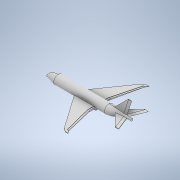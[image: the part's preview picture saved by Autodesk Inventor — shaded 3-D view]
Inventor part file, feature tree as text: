
AUTODESK INVENTOR PART (.ipt)
format: ipt  version: 2021 (Build 250183000, 183)  size: 514,560 bytes
history: native  units: in
note: dims shown in document units (in); Inventor stores cm internally (conversion verified against a paired STEP export)
features: sketch x11, extrude x5, plane x4, chamfer x4, projected_geometry x4, revolve x2, loft x2, mirror x2, fillet x2, other x2
ambient origin geometry x8: Origin, YZ Plane, XZ Plane, XY Plane, X Axis, Y Axis, Z Axis, Center Point
bodies: Solid1 (feature_tree)
feature tree (38):
  revolve  "Revolution1"  [1 undecoded]
  sketch  "Sketch2"  dims[d2=98.4252in d3=1456.6929in]
  plane  "Work Plane1"
  loft  "Loft1"
  revolve  "Revolution2"  [1 undecoded]
  sketch  "Sketch5"  dims[d9=984.252in d10=68.8976in]
  plane  "Work Plane2"
  loft  "Loft2"
  plane  "Work Plane3"
  extrude  "Extrusion1"  Depth=68.8976in
  extrude  "Extrusion2"  TaperAngle=0.0deg  [1 undecoded]
  extrude  "Extrusion3"  TaperAngle=0.0deg  [1 undecoded]
  extrude  "Extrusion4"  Depth=39.3701in
  chamfer  "Chamfer1"  Distance=64.18in
  chamfer  "Chamfer2"  Angle=90.0deg  [1 undecoded]
  plane  "Work Plane4"
  extrude  "Extrusion5"  TaperAngle=0.0deg  [1 undecoded]
  chamfer  "Chamfer3"  Angle=90.0deg  [1 undecoded]
  chamfer  "Chamfer4"  Distance=196.8504in
  mirror  "Mirror1"
  mirror  "Mirror2"
  fillet  "Fillet1"  Radius=590.5512in
  fillet  "Fillet2"  Radius=1181.1024in
  sketch  "Sketch1"  dims[d0=393.7008in d1=255.9055in]
  sketch  "Sketch3"  dims[d4=90.0deg d6=118.1102in]
  other  "Edges1"
  sketch  "Sketch4"  dims[d7=385.2643in d8=68.8976in]
  sketch  "Sketch6"  dims[d11=0.0in d12=90.0deg d13=0.0in d14=90.0deg]
  other  "Edges2"
  sketch  "Sketch7"  dims[d15=0.0in d16=90.0deg d17=0.0in d18=90.0deg]
  projected_geometry  "Projected Loop1"
  sketch  "Sketch8"  dims[d19=39.3701in d20=59.0551in]
  projected_geometry  "Projected Loop2"
  sketch  "Sketch9"  dims[d21=90.0deg]
  projected_geometry  "Projected Loop3"
  sketch  "Sketch10"  dims[d23=328.7402in]
  sketch  "Sketch11"  dims[d25=39.3701in d27=64.18in d28=0.0in d29=90.0deg d30=0.0in d31=90.0deg d32=0.0in d33=90.0deg d34=196.8504in d35=590.5512in d36=1181.1024in d37=0.3779in d38=118.1102in d39=1.0994in d40=78.7402in d41=118.1102in d42=590.5512in d43=295.2756in d44=98.4252in d45=0.0in d46=52.1654in d47=9.8425in d48=1242.1127in d49=0.0in d50=39.3701in d51=9.8425in d52=0.0in d53=354.3307in d54=167.3228in d55=29.5276in d56=590.5512in d57=45.0deg d58=98.4252in d59=19.685in d60=0.0in d61=78.7402in d62=9.8425in d63=45.0deg d64=78.7402in d65=9.8425in d66=45.0deg d67=300.2067in d68=354.3307in d69=118.1102in d70=118.1102in d71=590.5512in d72=98.4252in d73=45.0deg d74=19.685in d75=0.0in d76=78.7402in d77=9.8425in d78=45.0deg d79=78.7402in d80=9.8425in d81=45.0deg d82=39.3701in d83=39.3701in d5=0.0344in]
  projected_geometry  "Projected Loop4"
note: 7 required parameter values undecoded (feature->parameter linkage not recoverable at this tier; creation-order binding heuristic only, values carry confidence <= 0.55)